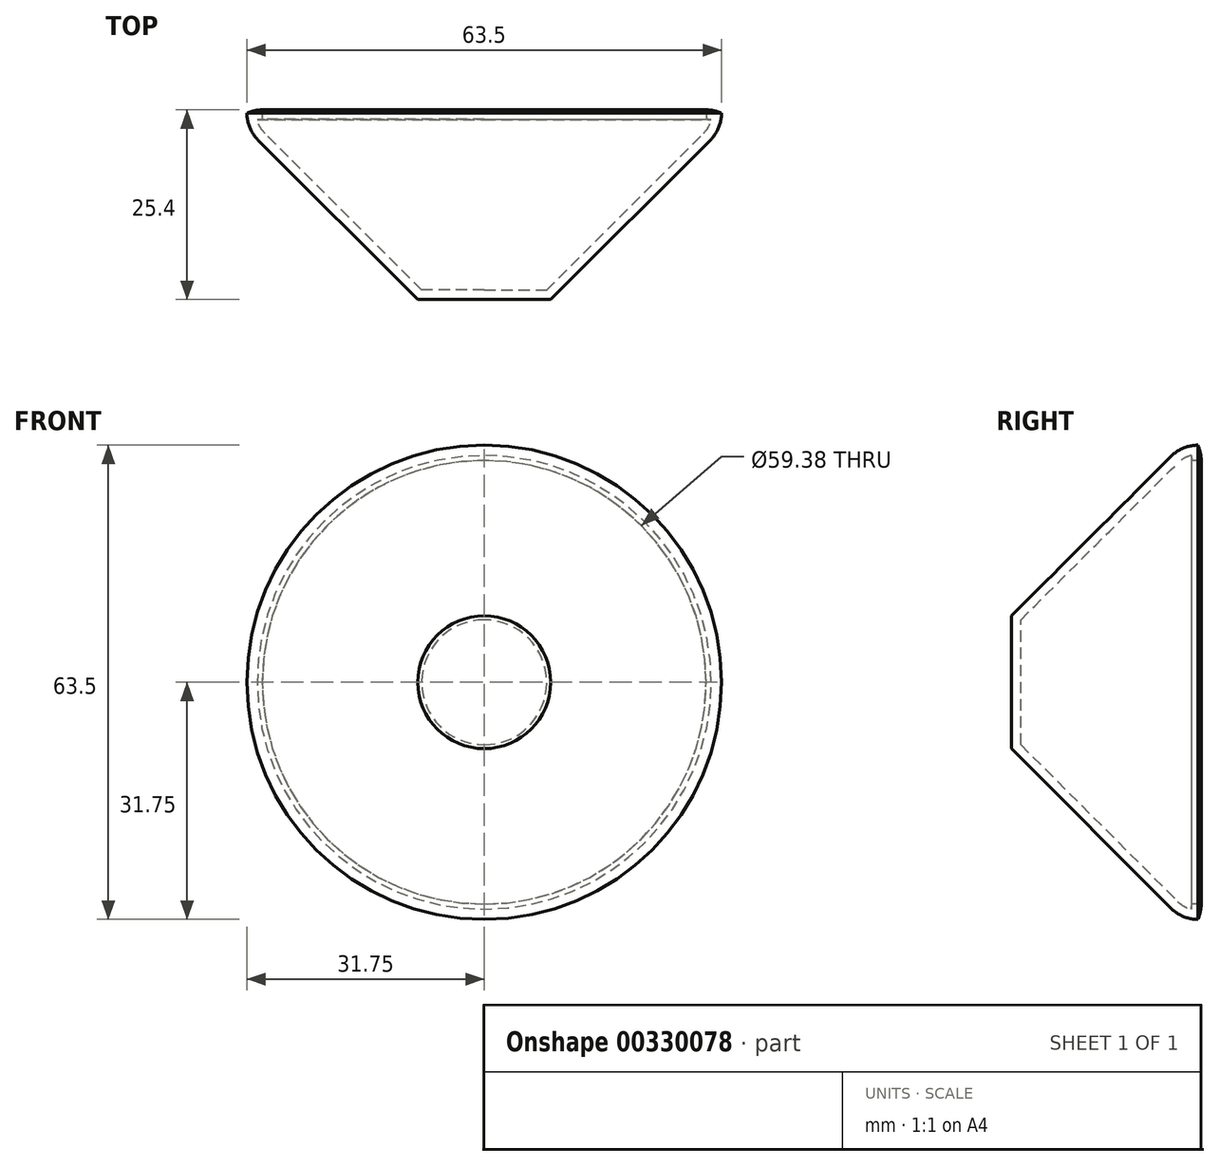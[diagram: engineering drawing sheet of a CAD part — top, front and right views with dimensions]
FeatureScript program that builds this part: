
annotation { "Feature Type Name" : "Feature", "Feature Type Description" : "" }
export const myFeature = defineFeature(function(context is Context, id is Id, definition is map)
    precondition{}
    {
        {
            var Q0;
            Q0=qCreatedBy(makeId("Front.planeOp"),FACE);
            var sketch = newSketch(context, id + "F0", { "sketchPlane" : qUnion([Q0])});
            skCircle(sketch, "E0", {"center": v(0, 0) * mm, "radius": 31.75 * mm});
            skSolve(sketch);
        }
        {
            var Q0;
            Q0=makeQuery(id+"F0.imprint","IMPRINT",FACE,{"disambiguationData":[TD([[makeQuery(id+"F0.imprint","IMPRINT",EDGE,{"derivedFrom":sQuery(id+"F0.wireOp",EDGE,"E0")}),1.0]])]});
            extrude(context, id + "F1", {"entities" : qUnion([Q0]), "depth" : 25.4 * mm});
        }
        {
            var Q0;
            Q0=makeQuery(id+"F1.opExtrude","CAP_EDGE",EDGE,{"disambiguationData":[OSD([sQuery(id+"F0.wireOp",EDGE,"E0")])],"isStart":false});
            chamfer(context, id + "F2", {"entities" : qUnion([Q0]), "width" : 22.86 * mm, "tangentPropagation" : true});
        }
        {
            var Q0;
            {var subQ0=sQuery(id+"F0.wireOp",EDGE,"E0");Q0=makeQuery(id+"F2.opChamfer","BLEND_EDGE",EDGE,{"blendedFrom":[makeQuery(id+"F1.opExtrude","CAP_EDGE",EDGE,{"disambiguationData":[OSD([subQ0])],"isStart":false}),makeQuery(id+"F1.opExtrude","SWEPT_FACE",FACE,{"disambiguationData":[OSD([subQ0])]})],"blendedInto":[makeQuery(id+"F1.opExtrude","SWEPT_FACE",FACE,{"disambiguationData":[OSD([subQ0])]})]});}
            fillet(context, id + "F3", {"entities" : qUnion([Q0]), "radius" : 5.08 * mm, "tangentPropagation" : true, "allowEdgeOverflow" : false});
        }
        {
            var Q0;
            Q0=makeQuery(id+"F1.opExtrude","CAP_EDGE",EDGE,{"disambiguationData":[OSD([sQuery(id+"F0.wireOp",EDGE,"E0")])],"isStart":true});
            fillet(context, id + "F4", {"entities" : qUnion([Q0]), "radius" : 5.08 * mm, "tangentPropagation" : true, "allowEdgeOverflow" : false});
        }
        {
            var Q0;
            Q0=makeQuery(id+"F1.opExtrude","CAP_FACE",FACE,{"disambiguationData":[OSD([sQuery(id+"F0.wireOp",EDGE,"E0")])],"isStart":true});
            shell(context, id + "F5", {"entities" : qUnion([Q0]), "thickness" : 1.27 * mm});
        }
    });
